# Revit family: РОСМА_Манометр_IP54
name_source: partatom
category: Арматура трубопроводов
revit_build: Autodesk Revit 2018 (Build: 20180423_1000(x64)
units: mm (PartAtom-declared; Revit-internal decimal feet)

## family parameters
Всегда вертикально = Да
На основе рабочей плоскости = Нет
Общий = Нет
При загрузке вырезать с полостями = Нет
Размер круглого соединителя = Использовать диаметр
Тип детали = Вставляется

## types (2) — shared parameters
ADSK_Единица измерения = шт.
ADSK_Количество = 1
DN = 15.00 мм
G = 20 мм
Lgol = 2 мм
Lrezba = 15 мм
S = 17 мм
Table = Размеры_10серияIP54
Table_2 = Спец_10серияIP54
URL = https://rosma.spb.ru
f = 18 мм
h гайки = 17 мм
Группа модели = Оборудование
Давление01 = ‎ : ТВ -0,1…0МПа
Давление03 = ‎ : ТМ 0…0,1МПа
Давление04 = ‎ : ТМ 0…0,16МПа
Давление05 = ‎ : ТМ 0…0,25МПа
Давление06 = ‎ : ТМ 0…0,4МПа
Давление07 = ‎ : ТМ 0…0,6МПа
Давление08 = ‎ : ТМ 0…1,0МПа
Давление09 = ‎ : ТМ 0…1,6МПа
Давление10 = ‎ : ТМ 0…2,5МПа
Давление11 = ‎ : ТМ 0…4МПа
Давление12 = ‎ : ТМ 0…6МПа
Давление13 = ‎ : ТМ 0…10МПа
Давление14 = ‎ : ТМ 0…16МПа
Давление15 = ‎ : ТМ 0…25МПа
Давление16 = ‎ : ТМ 0…40МПа
Давление17 = ‎ : ТМ 0…60МПа
Давление18 = ‎ : ТМ 0…100МПа
Давление19 = ‎ : ТМВ -0,1…0,15МПа
Давление20 = ‎ : ТМВ -0,1…0,3МПа
Давление21 = ‎ : ТМВ -0,1…0,5МПа
Давление22 = ‎ : ТМВ -0,1…0,9МПа
Давление23 = ‎ : ТМВ -0,1…1,5МПа
Давление24 = ‎ : ТМВ -0,1…2,4МПа
Изготовитель = ЗАО "РОСМА"
Класс точности = 1,5
Климатическое исполнение = Группа Д2 по ГОСТ Р 52931; климатическое исполнение УХЛ категории 1.1 по ГОСТ 15150
Код IP = IP54
Межповерочный интервал = 2 года
Описание = Манометр показывающий ТМ серия 10, с повышенной  пылевлагозащищенностью.
Присоединение = Радиальное
Техническая документация = ТУ 4212-001-4719015564-2008; ГОСТ 2405–88

## per-type parameters (varying)
| type | ADSK_Масса_Текст | D | D1 | D2 | Drezba | R1 шкала | R2 шкала | R_Logo | b | b-e | e | h | Длина стрелки |
| 610 | 0,71 | 150 мм | 152 мм | 148 мм | M20 | 60 мм | 58 мм | 51 мм | 48 мм | 25 мм | 23 мм | 110 мм | 56 мм |
| 510 | 0,39 | 100 мм | 100 мм | 98 мм |  | 35 мм | 33 мм | 26 мм | 46 мм | 24 мм | 22 мм | 85 мм | 31 мм |

note: column(s) folded — value = type name in every type: Исполнение
